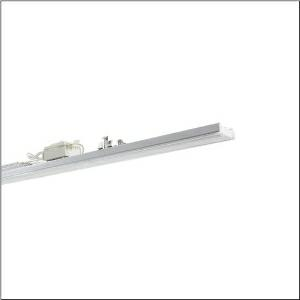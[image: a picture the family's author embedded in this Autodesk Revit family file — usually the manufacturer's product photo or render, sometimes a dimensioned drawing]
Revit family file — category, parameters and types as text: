
# Revit family: licross_r__21_recessed_mo_52te10dn4axg_60c1
name_source: partatom
category: Lighting Fixtures
units: mm (PartAtom-declared; Revit-internal decimal feet)

## family parameters
Cut with Voids When Loaded = No
Host = Face
Light Source = No
Part Type = Normal
Room Calculation Point = No
Round Connector Dimension = Use Diameter
Shared = No

## types (1)
- --- (1 x LED, 10000 lm, 58 W, 4000K)
    Apparent Load = 58 VA
    CIE Flux Codes = 50 81 96 100 100
    Color Rendering = 80
    Color Temperature = 4000K
    Default Elevation = 1800 mm
    Description = Licross® 21 Recessed MO, luminaire insert, of sheet steel, galvanised, coil coated, white, length: 1.500mm, width: 66mm, height: 67mm, LED rated luminous flux: 10.000lm, light colour: 840, control gear: DALI 2, with plug, 5-pole, with phase selection, mains connection: 220..240V, AC, 50/60Hz, rated input power: 58W, halogen-free wiring, primary optical cover: cover, of PMMA, light emission: direct distribution, primary light characteristic: symmetric, protection rating (complete): IP54, insulation class (complete): insulation class I (protective earthing), certification: CE, ENEC, VDE, UKCA, protection symbol: D if used in an environment with non-conductive dust loads with corresponding accessories, impact resistance: IK06, permissible ambient temperature for indoor applications: -25..+35°C, corresponds to IFS (International Featured Standards) requirements for safety and quality in the food industry, reducing of maximum allowable ambient temperature of 5°C with ceiling mounting, LABS conformity tested according to VDMA 24364:2018-05, packaging unit: 1 piece
    Height = 58 mm
    Lamp = 1 x LED
    Lamp Light Flux = 10000 lm
    Lamp Power = 58 W
    Lamp count = 1
    Length = 1500 mm
    Luminous efficacy = 172 lm/W
    Manufacturer = Siteco
    ModVariant = No
    Model = 52TE10DN4AXG
    Mounting Place = Ceiling
    Mounting Type = Pendant
    Number of Poles = 1
    OnlyDefault = Yes
    Power Factor = 1
    Product Name = Licross® 21 Recessed MO
    Product group = luminaire insert
    ProductGroupID = 902
    Protection Class = Protection class I
    Protection Degree = IP 54
    RLX_Detail_Level = 1
    RLX_Emergency_Light_Flux = 0 lm
    RLX_Emergency_Type = 0
    RLX_Emergency_Type_DB = No
    RlxData = <blob elided: 24365 chars, md5=224635e8>
    Socket = socket
    Standby Power = 0 W
    System Light Flux = 10000 lm
    System Power = 58 W
    Type Comments = factory setting: luminous flux: 100 % | dim-lin: 254 | 390 mA
    Type Image = l_1296930.jpg
    URL = http://relux.com
    VarID = @adj_127508
    Voltage = 0 V
    Weight = 0.00 kg
    Width = 66 mm

## geometry (parser evidence)
native form markers: Blend x4, Sweep x13
no freeform markers — native parametric forms only
